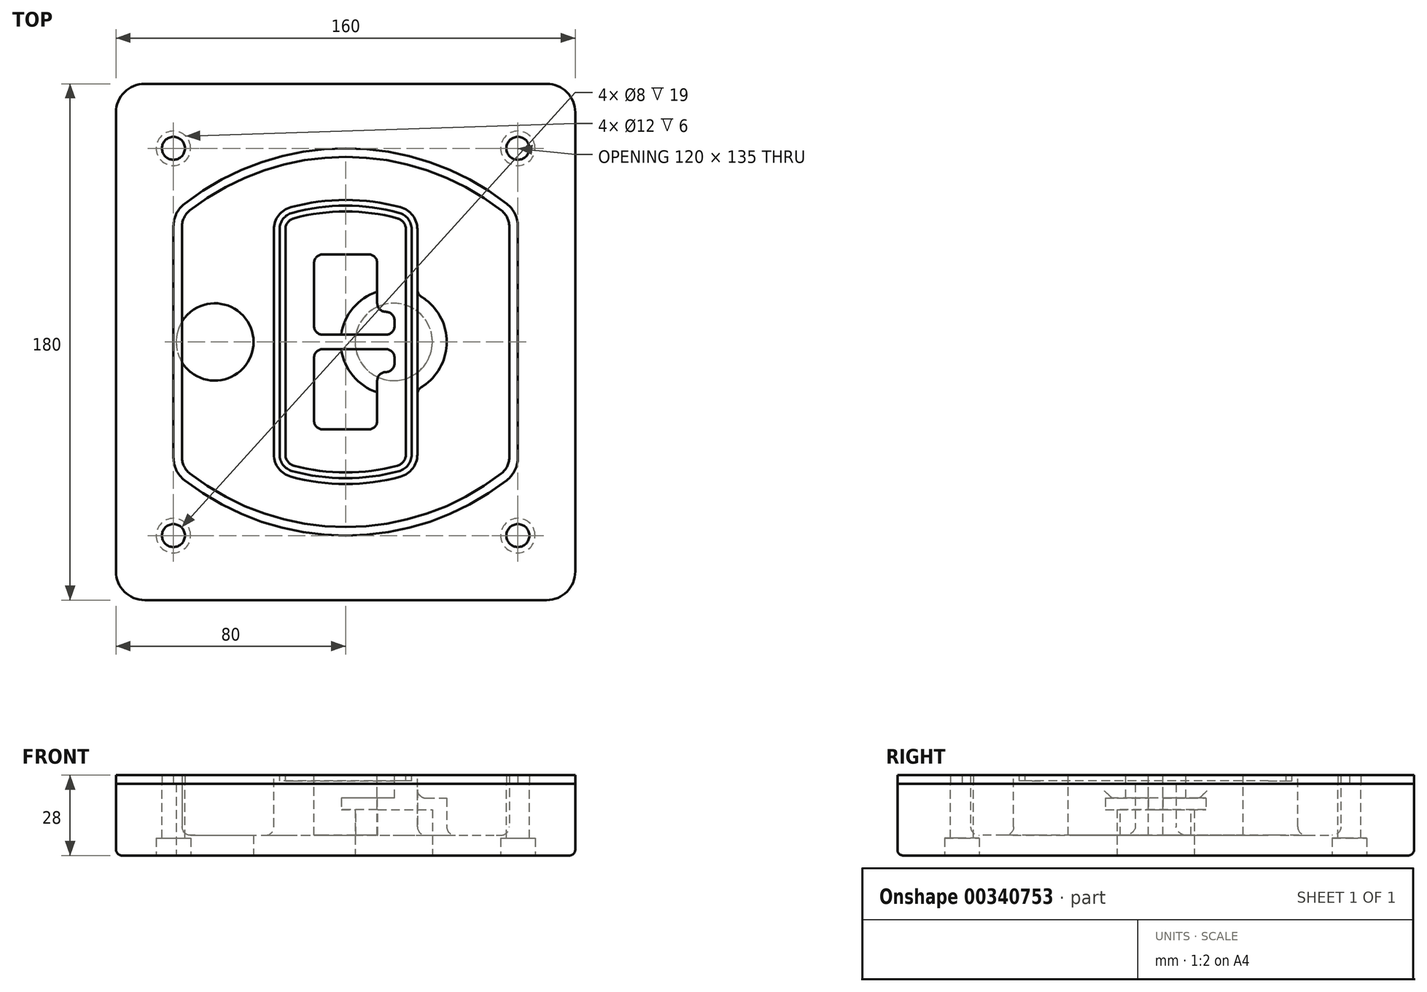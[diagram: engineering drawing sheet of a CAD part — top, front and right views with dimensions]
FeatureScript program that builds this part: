
annotation { "Feature Type Name" : "Feature", "Feature Type Description" : "" }
export const myFeature = defineFeature(function(context is Context, id is Id, definition is map)
    precondition{}
    {
        {
            var Q0;
            Q0=qCreatedBy(makeId("Top.planeOp"),FACE);
            var sketch = newSketch(context, id + "F0", { "sketchPlane" : qUnion([Q0])});
            skPoint(sketch, "E0.rect.middle", {"position": v(0, 0) * mm});
            skLineSegment(sketch, "E1.bottom", {"start": v(-70, -90) * mm, "end": v(70, -90) * mm});
            skLineSegment(sketch, "E1.top", {"start": v(-70, 90) * mm, "end": v(70, 90) * mm});
            skLineSegment(sketch, "E1.left", {"start": v(-80, -80) * mm, "end": v(-80, 80) * mm});
            skLineSegment(sketch, "E1.right", {"start": v(80, -80) * mm, "end": v(80, 80) * mm});
            skLineSegment(sketch, "E2", {"start": v(-80, 90) * mm, "end": v(80, -90) * mm, "construction": true});
            skLineSegment(sketch, "E3", {"start": v(80, 90) * mm, "end": v(-80, -90) * mm, "construction": true});
            skCircle(sketch, "E4", {"center": v(-60, 67.5) * mm, "radius": 4 * mm});
            skCircle(sketch, "E5", {"center": v(60, 67.5) * mm, "radius": 4 * mm});
            skCircle(sketch, "E6", {"center": v(60, -67.5) * mm, "radius": 4 * mm});
            skCircle(sketch, "E7", {"center": v(-60, -67.5) * mm, "radius": 4 * mm});
            skLineSegment(sketch, "E8", {"start": v(-60, 67.5) * mm, "end": v(60, 67.5) * mm, "construction": true});
            skLineSegment(sketch, "E9", {"start": v(60, 67.5) * mm, "end": v(60, -67.5) * mm, "construction": true});
            skLineSegment(sketch, "E10", {"start": v(60, -67.5) * mm, "end": v(-60, -67.5) * mm, "construction": true});
            skLineSegment(sketch, "E11", {"start": v(-60, -67.5) * mm, "end": v(-60, 67.5) * mm, "construction": true});
            skLineSegment(sketch, "E12", {"start": v(-60, 40.3) * mm, "end": v(-60, -40.3) * mm});
            skLineSegment(sketch, "E13", {"start": v(60, 40.3) * mm, "end": v(60, -40.3) * mm});
            skArc(sketch, "E14", {"start": v(56.15, 48.18) * mm, "mid": v(0, 67.5) * mm, "end": v(-56.15, 48.18) * mm});
            skArc(sketch, "E15", {"start": v(-56.15, -48.18) * mm, "mid": v(0, -67.5) * mm, "end": v(56.15, -48.18) * mm});
            skLineSegment(sketch, "E16", {"start": v(-60, 0) * mm, "end": v(60, 0) * mm, "construction": true});
            skPoint(sketch, "E17.visualSharp", {"position": v(-60, -45) * mm});
            skArc(sketch, "E17.filletArc", {"start": v(-60, -40.3) * mm, "mid": v(-58.99, -44.68) * mm, "end": v(-56.15, -48.18) * mm});
            skPoint(sketch, "E18.visualSharp", {"position": v(-60, 45) * mm});
            skArc(sketch, "E18.filletArc", {"start": v(-56.15, 48.18) * mm, "mid": v(-58.99, 44.68) * mm, "end": v(-60, 40.3) * mm});
            skPoint(sketch, "E19.visualSharp", {"position": v(60, 45) * mm});
            skArc(sketch, "E19.filletArc", {"start": v(60, 40.3) * mm, "mid": v(58.99, 44.68) * mm, "end": v(56.15, 48.18) * mm});
            skPoint(sketch, "E20.visualSharp", {"position": v(60, -45) * mm});
            skArc(sketch, "E20.filletArc", {"start": v(56.15, -48.18) * mm, "mid": v(58.99, -44.68) * mm, "end": v(60, -40.3) * mm});
            skPoint(sketch, "E21.visualSharp", {"position": v(-80, 90) * mm});
            skArc(sketch, "E21.filletArc", {"start": v(-70, 90) * mm, "mid": v(-77.07, 87.07) * mm, "end": v(-80, 80) * mm});
            skPoint(sketch, "E22.visualSharp", {"position": v(80, 90) * mm});
            skArc(sketch, "E22.filletArc", {"start": v(80, 80) * mm, "mid": v(77.07, 87.07) * mm, "end": v(70, 90) * mm});
            skPoint(sketch, "E23.visualSharp", {"position": v(80, -90) * mm});
            skArc(sketch, "E23.filletArc", {"start": v(70, -90) * mm, "mid": v(77.07, -87.07) * mm, "end": v(80, -80) * mm});
            skPoint(sketch, "E24.visualSharp", {"position": v(-80, -90) * mm});
            skArc(sketch, "E24.filletArc", {"start": v(-80, -80) * mm, "mid": v(-77.07, -87.07) * mm, "end": v(-70, -90) * mm});
            skArc(sketch, "E25.0", {"start": v(57, 40.3) * mm, "mid": v(56.3, 43.36) * mm, "end": v(54.3, 45.81) * mm});
            skLineSegment(sketch, "E25.1", {"start": v(57, 40.3) * mm, "end": v(57, -40.3) * mm});
            skArc(sketch, "E25.2", {"start": v(54.3, -45.81) * mm, "mid": v(56.3, -43.36) * mm, "end": v(57, -40.3) * mm});
            skArc(sketch, "E25.3", {"start": v(-54.3, -45.81) * mm, "mid": v(0, -64.5) * mm, "end": v(54.3, -45.81) * mm});
            skArc(sketch, "E25.4", {"start": v(-57, -40.3) * mm, "mid": v(-56.3, -43.36) * mm, "end": v(-54.3, -45.81) * mm});
            skArc(sketch, "E25.5", {"start": v(54.3, 45.81) * mm, "mid": v(0, 64.5) * mm, "end": v(-54.3, 45.81) * mm});
            skLineSegment(sketch, "E25.6", {"start": v(-57, 40.3) * mm, "end": v(-57, -40.3) * mm});
            skArc(sketch, "E25.7", {"start": v(-54.3, 45.81) * mm, "mid": v(-56.3, 43.36) * mm, "end": v(-57, 40.3) * mm});
            skArc(sketch, "E26.0", {"start": v(-58.62, 51.33) * mm, "mid": v(-62.58, 46.43) * mm, "end": v(-64, 40.3) * mm});
            skArc(sketch, "E26.1", {"start": v(58.62, 51.33) * mm, "mid": v(0, 71.5) * mm, "end": v(-58.62, 51.33) * mm});
            skArc(sketch, "E26.2", {"start": v(64, 40.3) * mm, "mid": v(62.58, 46.43) * mm, "end": v(58.62, 51.33) * mm});
            skLineSegment(sketch, "E26.3", {"start": v(64, 40.3) * mm, "end": v(64, -40.3) * mm});
            skArc(sketch, "E26.4", {"start": v(58.62, -51.33) * mm, "mid": v(62.58, -46.43) * mm, "end": v(64, -40.3) * mm});
            skLineSegment(sketch, "E26.5", {"start": v(-64, 40.3) * mm, "end": v(-64, -40.3) * mm});
            skArc(sketch, "E26.6", {"start": v(-58.62, -51.33) * mm, "mid": v(0, -71.5) * mm, "end": v(58.62, -51.33) * mm});
            skArc(sketch, "E26.7", {"start": v(-64, -40.3) * mm, "mid": v(-62.58, -46.43) * mm, "end": v(-58.62, -51.33) * mm});
            skSolve(sketch);
        }
        {
            var Q0;
            Q0=makeQuery(id+"F0.imprint","IMPRINT",FACE,{"disambiguationData":[TD([[makeQuery(id+"F0.imprint","IMPRINT",EDGE,{"derivedFrom":sQuery(id+"F0.wireOp",EDGE,"E1.bottom")}),1.0]])]});
            var Q1;
            Q1=makeQuery(id+"F0.imprint","IMPRINT",FACE,{"disambiguationData":[TD([[makeQuery(id+"F0.imprint","IMPRINT",EDGE,{"derivedFrom":sQuery(id+"F0.wireOp",EDGE,"E12")}),1.0]])]});
            var Q2;
            Q2=makeQuery(id+"F0.imprint","IMPRINT",FACE,{"disambiguationData":[TD([[makeQuery(id+"F0.imprint","IMPRINT",EDGE,{"derivedFrom":sQuery(id+"F0.wireOp",EDGE,"E25.0")}),1.0]])]});
            var Q3;
            Q3=makeQuery(id+"F0.imprint","IMPRINT",FACE,{"disambiguationData":[TD([[makeQuery(id+"F0.imprint","IMPRINT",EDGE,{"derivedFrom":sQuery(id+"F0.wireOp",EDGE,"E12")}),-1.0]])]});
            extrude(context, id + "F1", {"entities" : qUnion([Q0, Q1, Q2, Q3]), "oppositeDirection" : true, "depth" : 25 * mm});
        }
        {
            var Q0;
            Q0=makeQuery(id+"F0.imprint","IMPRINT",FACE,{"disambiguationData":[TD([[makeQuery(id+"F0.imprint","IMPRINT",EDGE,{"derivedFrom":sQuery(id+"F0.wireOp",EDGE,"E12")}),1.0]])]});
            extrude(context, id + "F2", {"entities" : qUnion([Q0]), "operationType" : NewBodyOperationType.ADD, "depth" : 3 * mm});
        }
        {
            var Q0;
            Q0=makeQuery(id+"F0.imprint","IMPRINT",FACE,{"disambiguationData":[TD([[makeQuery(id+"F0.imprint","IMPRINT",EDGE,{"derivedFrom":sQuery(id+"F0.wireOp",EDGE,"E25.0")}),1.0]])]});
            extrude(context, id + "F3", {"entities" : qUnion([Q0]), "operationType" : NewBodyOperationType.REMOVE, "oppositeDirection" : true, "depth" : 18 * mm});
        }
        {
            var Q0;
            Q0=makeQuery(id+"F2.opExtrude","CAP_FACE",FACE,{"disambiguationData":[OSD([sQuery(id+"F0.wireOp",EDGE,"E12"),sQuery(id+"F0.wireOp",EDGE,"E13"),sQuery(id+"F0.wireOp",EDGE,"E14"),sQuery(id+"F0.wireOp",EDGE,"E15"),sQuery(id+"F0.wireOp",EDGE,"E17.filletArc"),sQuery(id+"F0.wireOp",EDGE,"E18.filletArc"),sQuery(id+"F0.wireOp",EDGE,"E19.filletArc"),sQuery(id+"F0.wireOp",EDGE,"E20.filletArc"),sQuery(id+"F0.wireOp",EDGE,"E25.0"),sQuery(id+"F0.wireOp",EDGE,"E25.1"),sQuery(id+"F0.wireOp",EDGE,"E25.2"),sQuery(id+"F0.wireOp",EDGE,"E25.3"),sQuery(id+"F0.wireOp",EDGE,"E25.4"),sQuery(id+"F0.wireOp",EDGE,"E25.5"),sQuery(id+"F0.wireOp",EDGE,"E25.6"),sQuery(id+"F0.wireOp",EDGE,"E25.7")])],"isStart":false});
            var sketch = newSketch(context, id + "F4", { "sketchPlane" : qUnion([Q0])});
            skArc(sketch, "E27.0", {"start": v(-19.08, -46.97) * mm, "mid": v(0, -49.5) * mm, "end": v(19.08, -46.97) * mm});
            skArc(sketch, "E28.0", {"start": v(19.08, 46.97) * mm, "mid": v(0, 49.5) * mm, "end": v(-19.08, 46.97) * mm});
            skLineSegment(sketch, "E29", {"start": v(-25, 39.25) * mm, "end": v(-25, -39.25) * mm});
            skLineSegment(sketch, "E30", {"start": v(25, 39.25) * mm, "end": v(25, -39.25) * mm});
            skLineSegment(sketch, "E31", {"start": v(-25, 45.1) * mm, "end": v(25, 45.1) * mm, "construction": true});
            skLineSegment(sketch, "E32", {"start": v(-25, -45.1) * mm, "end": v(25, -45.1) * mm, "construction": true});
            skPoint(sketch, "E33.visualSharp", {"position": v(-25, 45.1) * mm});
            skArc(sketch, "E33.filletArc", {"start": v(-19.08, 46.97) * mm, "mid": v(-23.35, 44.11) * mm, "end": v(-25, 39.25) * mm});
            skPoint(sketch, "E34.visualSharp", {"position": v(25, 45.1) * mm});
            skArc(sketch, "E34.filletArc", {"start": v(25, 39.25) * mm, "mid": v(23.35, 44.11) * mm, "end": v(19.08, 46.97) * mm});
            skPoint(sketch, "E35.visualSharp", {"position": v(25, -45.1) * mm});
            skArc(sketch, "E35.filletArc", {"start": v(19.08, -46.97) * mm, "mid": v(23.35, -44.11) * mm, "end": v(25, -39.25) * mm});
            skPoint(sketch, "E36.visualSharp", {"position": v(-25, -45.1) * mm});
            skArc(sketch, "E36.filletArc", {"start": v(-25, -39.25) * mm, "mid": v(-23.35, -44.11) * mm, "end": v(-19.08, -46.97) * mm});
            skArc(sketch, "E37.0", {"start": v(54.3, 45.81) * mm, "mid": v(0, 64.5) * mm, "end": v(-54.3, 45.81) * mm});
            skArc(sketch, "E37.1", {"start": v(-54.3, 45.81) * mm, "mid": v(-56.3, 43.36) * mm, "end": v(-57, 40.3) * mm});
            skLineSegment(sketch, "E37.2", {"start": v(-57, 40.3) * mm, "end": v(-57, -40.3) * mm});
            skArc(sketch, "E37.3", {"start": v(-57, -40.3) * mm, "mid": v(-56.3, -43.36) * mm, "end": v(-54.3, -45.81) * mm});
            skArc(sketch, "E37.4", {"start": v(-54.3, -45.81) * mm, "mid": v(0, -64.5) * mm, "end": v(54.3, -45.81) * mm});
            skArc(sketch, "E37.5", {"start": v(54.3, -45.81) * mm, "mid": v(56.3, -43.36) * mm, "end": v(57, -40.3) * mm});
            skLineSegment(sketch, "E37.6", {"start": v(57, 40.3) * mm, "end": v(57, -40.3) * mm});
            skArc(sketch, "E37.7", {"start": v(57, 40.3) * mm, "mid": v(56.3, 43.36) * mm, "end": v(54.3, 45.81) * mm});
            skLineSegment(sketch, "E38.0", {"start": v(23, 39.25) * mm, "end": v(23, -39.25) * mm});
            skArc(sketch, "E38.1", {"start": v(18.56, -45.04) * mm, "mid": v(21.76, -42.9) * mm, "end": v(23, -39.25) * mm});
            skArc(sketch, "E38.2", {"start": v(-18.56, -45.04) * mm, "mid": v(0, -47.5) * mm, "end": v(18.56, -45.04) * mm});
            skArc(sketch, "E38.3", {"start": v(-23, -39.25) * mm, "mid": v(-21.76, -42.9) * mm, "end": v(-18.56, -45.04) * mm});
            skLineSegment(sketch, "E38.4", {"start": v(-23, 39.25) * mm, "end": v(-23, -39.25) * mm});
            skArc(sketch, "E38.5", {"start": v(23, 39.25) * mm, "mid": v(21.76, 42.9) * mm, "end": v(18.56, 45.04) * mm});
            skArc(sketch, "E38.6", {"start": v(-18.56, 45.04) * mm, "mid": v(-21.76, 42.9) * mm, "end": v(-23, 39.25) * mm});
            skArc(sketch, "E38.7", {"start": v(18.56, 45.04) * mm, "mid": v(0, 47.5) * mm, "end": v(-18.56, 45.04) * mm});
            skArc(sketch, "E39.0", {"start": v(21, 39.25) * mm, "mid": v(20.18, 41.68) * mm, "end": v(18.04, 43.1) * mm});
            skLineSegment(sketch, "E39.1", {"start": v(21, 39.25) * mm, "end": v(21, -39.25) * mm});
            skArc(sketch, "E39.2", {"start": v(18.04, -43.1) * mm, "mid": v(20.18, -41.68) * mm, "end": v(21, -39.25) * mm});
            skArc(sketch, "E39.3", {"start": v(-18.04, -43.1) * mm, "mid": v(0, -45.5) * mm, "end": v(18.04, -43.1) * mm});
            skArc(sketch, "E39.4", {"start": v(-21, -39.25) * mm, "mid": v(-20.18, -41.68) * mm, "end": v(-18.04, -43.1) * mm});
            skArc(sketch, "E39.5", {"start": v(18.04, 43.1) * mm, "mid": v(0, 45.5) * mm, "end": v(-18.04, 43.1) * mm});
            skLineSegment(sketch, "E39.6", {"start": v(-21, 39.25) * mm, "end": v(-21, -39.25) * mm});
            skArc(sketch, "E39.7", {"start": v(-18.04, 43.1) * mm, "mid": v(-20.18, 41.68) * mm, "end": v(-21, 39.25) * mm});
            skLineSegment(sketch, "E40", {"start": v(-25, 0) * mm, "end": v(25, 0) * mm, "construction": true});
            skLineSegment(sketch, "E41", {"start": v(-11, 5.5) * mm, "end": v(-11, 27.5) * mm});
            skLineSegment(sketch, "E42", {"start": v(-8, 30.5) * mm, "end": v(8, 30.5) * mm});
            skLineSegment(sketch, "E43", {"start": v(11, 27.5) * mm, "end": v(11, 13.5) * mm});
            skLineSegment(sketch, "E44", {"start": v(14, 10.5) * mm, "end": v(14, 10.5) * mm});
            skLineSegment(sketch, "E45", {"start": v(17, 7.5) * mm, "end": v(17, 5.5) * mm});
            skLineSegment(sketch, "E46", {"start": v(14, 2.5) * mm, "end": v(-8, 2.5) * mm});
            skPoint(sketch, "E47.visualSharp", {"position": v(-11, 30.5) * mm});
            skArc(sketch, "E47.filletArc", {"start": v(-8, 30.5) * mm, "mid": v(-10.12, 29.62) * mm, "end": v(-11, 27.5) * mm});
            skPoint(sketch, "E48.visualSharp", {"position": v(11, 30.5) * mm});
            skArc(sketch, "E48.filletArc", {"start": v(11, 27.5) * mm, "mid": v(10.12, 29.62) * mm, "end": v(8, 30.5) * mm});
            skPoint(sketch, "E49.visualSharp", {"position": v(11, 10.5) * mm});
            skArc(sketch, "E49.filletArc", {"start": v(11, 13.5) * mm, "mid": v(11.88, 11.38) * mm, "end": v(14, 10.5) * mm});
            skPoint(sketch, "E50.visualSharp", {"position": v(17, 10.5) * mm});
            skArc(sketch, "E50.filletArc", {"start": v(17, 7.5) * mm, "mid": v(16.12, 9.62) * mm, "end": v(14, 10.5) * mm});
            skPoint(sketch, "E51.visualSharp", {"position": v(17, 2.5) * mm});
            skArc(sketch, "E51.filletArc", {"start": v(14, 2.5) * mm, "mid": v(16.12, 3.38) * mm, "end": v(17, 5.5) * mm});
            skPoint(sketch, "E52.visualSharp", {"position": v(-11, 2.5) * mm});
            skArc(sketch, "E52.filletArc", {"start": v(-11, 5.5) * mm, "mid": v(-10.12, 3.38) * mm, "end": v(-8, 2.5) * mm});
            skLineSegment(sketch, "E53.0.MirrorCS", {"start": v(14, -2.5) * mm, "end": v(-8, -2.5) * mm});
            skArc(sketch, "E54.0.MirrorCS", {"start": v(-11, -5.5) * mm, "mid": v(-10.12, -3.38) * mm, "end": v(-8, -2.5) * mm});
            skLineSegment(sketch, "E55.0.MirrorCS", {"start": v(-11, -5.5) * mm, "end": v(-11, -27.5) * mm});
            skArc(sketch, "E56.0.MirrorCS", {"start": v(-8, -30.5) * mm, "mid": v(-10.12, -29.62) * mm, "end": v(-11, -27.5) * mm});
            skLineSegment(sketch, "E57.0.MirrorCS", {"start": v(-8, -30.5) * mm, "end": v(8, -30.5) * mm});
            skArc(sketch, "E58.0.MirrorCS", {"start": v(11, -27.5) * mm, "mid": v(10.12, -29.62) * mm, "end": v(8, -30.5) * mm});
            skLineSegment(sketch, "E59.0.MirrorCS", {"start": v(11, -27.5) * mm, "end": v(11, -13.5) * mm});
            skArc(sketch, "E60.0.MirrorCS", {"start": v(11, -13.5) * mm, "mid": v(11.88, -11.38) * mm, "end": v(14, -10.5) * mm});
            skArc(sketch, "E61.0.MirrorCS", {"start": v(17, -7.5) * mm, "mid": v(16.12, -9.62) * mm, "end": v(14, -10.5) * mm});
            skLineSegment(sketch, "E62.0.MirrorCS", {"start": v(17, -7.5) * mm, "end": v(17, -5.5) * mm});
            skArc(sketch, "E63.0.MirrorCS", {"start": v(14, -2.5) * mm, "mid": v(16.12, -3.38) * mm, "end": v(17, -5.5) * mm});
            skSolve(sketch);
        }
        {
            var Q0;
            Q0=makeQuery(id+"F4.imprint","IMPRINT",FACE,{"disambiguationData":[TD([[makeQuery(id+"F4.imprint","IMPRINT",EDGE,{"derivedFrom":sQuery(id+"F4.wireOp",EDGE,"E27.0")}),1.0]])]});
            var Q1;
            Q1=makeQuery(id+"F4.imprint","IMPRINT",FACE,{"disambiguationData":[TD([[makeQuery(id+"F4.imprint","IMPRINT",EDGE,{"derivedFrom":sQuery(id+"F4.wireOp",EDGE,"E38.0")}),-1.0]])]});
            var Q2;
            Q2=makeQuery(id+"F4.imprint","IMPRINT",FACE,{"disambiguationData":[TD([[makeQuery(id+"F4.imprint","IMPRINT",EDGE,{"derivedFrom":sQuery(id+"F4.wireOp",EDGE,"E39.0")}),1.0]])]});
            extrude(context, id + "F5", {"entities" : qUnion([Q0, Q1, Q2]), "operationType" : NewBodyOperationType.ADD, "endBound" : BoundingType.UP_TO_NEXT, "oppositeDirection" : true, "depth" : 25 * mm});
        }
        {
            var Q0;
            Q0=makeQuery(id+"F4.imprint","IMPRINT",FACE,{"disambiguationData":[TD([[makeQuery(id+"F4.imprint","IMPRINT",EDGE,{"derivedFrom":sQuery(id+"F4.wireOp",EDGE,"E38.0")}),-1.0]])]});
            extrude(context, id + "F6", {"entities" : qUnion([Q0]), "operationType" : NewBodyOperationType.REMOVE, "oppositeDirection" : true, "depth" : 2 * mm});
        }
        {
            var Q0;
            Q0=makeQuery(id+"F1.opExtrude","CAP_FACE",FACE,{"disambiguationData":[OSD([sQuery(id+"F0.wireOp",EDGE,"E1.bottom"),sQuery(id+"F0.wireOp",EDGE,"E1.top"),sQuery(id+"F0.wireOp",EDGE,"E1.left"),sQuery(id+"F0.wireOp",EDGE,"E1.right"),sQuery(id+"F0.wireOp",EDGE,"E4"),sQuery(id+"F0.wireOp",EDGE,"E5"),sQuery(id+"F0.wireOp",EDGE,"E6"),sQuery(id+"F0.wireOp",EDGE,"E7"),sQuery(id+"F0.wireOp",EDGE,"E21.filletArc"),sQuery(id+"F0.wireOp",EDGE,"E22.filletArc"),sQuery(id+"F0.wireOp",EDGE,"E23.filletArc"),sQuery(id+"F0.wireOp",EDGE,"E24.filletArc")])],"isStart":false});
            var sketch = newSketch(context, id + "F7", { "sketchPlane" : qUnion([Q0])});
            skCircle(sketch, "E64", {"center": v(16.76, 0) * mm, "radius": 13.47 * mm});
            skCircle(sketch, "E65", {"center": v(-45.56, 0) * mm, "radius": 13.47 * mm});
            skLineSegment(sketch, "E66", {"start": v(80, 0) * mm, "end": v(-80, 0) * mm});
            skCircle(sketch, "E67", {"center": v(16.76, 0) * mm, "radius": 18.47 * mm});
            skCircle(sketch, "E68", {"center": v(60, -67.5) * mm, "radius": 6 * mm});
            skCircle(sketch, "E69", {"center": v(-60, -67.5) * mm, "radius": 6 * mm});
            skCircle(sketch, "E70", {"center": v(-60, 67.5) * mm, "radius": 6 * mm});
            skCircle(sketch, "E71", {"center": v(60, 67.5) * mm, "radius": 6 * mm});
            skSolve(sketch);
        }
        {
            var Q0;
            {var subQ1=sQuery(id+"F7.wireOp",EDGE,"E66");var subQ4=sQuery(id+"F7.wireOp",EDGE,"E64");var subQ6=makeQuery(id+"F7.imprint","INTERSECT",VERTEX,{"disambiguationData":[OD(0.0)],"derivedFrom":[subQ4,subQ1]});Q0=makeQuery(id+"F7.imprint","IMPRINT",FACE,{"disambiguationData":[TD([[makeQuery(id+"F7.imprint","IMPRINT",EDGE,{"disambiguationData":[TD([[subQ6,-1.0]])],"derivedFrom":subQ4}),-1.0]])]});}
            var Q1;
            {var subQ0=sQuery(id+"F7.wireOp",EDGE,"E66");var subQ1=sQuery(id+"F7.wireOp",EDGE,"E64");var subQ3=makeQuery(id+"F7.imprint","INTERSECT",VERTEX,{"disambiguationData":[OD(0.0)],"derivedFrom":[subQ1,subQ0]});Q1=makeQuery(id+"F7.imprint","IMPRINT",FACE,{"disambiguationData":[TD([[makeQuery(id+"F7.imprint","IMPRINT",EDGE,{"disambiguationData":[TD([[subQ3,-1.0]])],"derivedFrom":subQ1}),1.0]])]});}
            var Q2;
            {var subQ0=sQuery(id+"F7.wireOp",EDGE,"E66");var subQ1=sQuery(id+"F7.wireOp",EDGE,"E64");var subQ3=makeQuery(id+"F7.imprint","INTERSECT",VERTEX,{"disambiguationData":[OD(0.0)],"derivedFrom":[subQ1,subQ0]});Q2=makeQuery(id+"F7.imprint","IMPRINT",FACE,{"disambiguationData":[TD([[makeQuery(id+"F7.imprint","IMPRINT",EDGE,{"disambiguationData":[TD([[subQ3,1.0]])],"derivedFrom":subQ1}),1.0]])]});}
            var Q3;
            {var subQ1=sQuery(id+"F7.wireOp",EDGE,"E66");var subQ4=sQuery(id+"F7.wireOp",EDGE,"E64");var subQ6=makeQuery(id+"F7.imprint","INTERSECT",VERTEX,{"disambiguationData":[OD(0.0)],"derivedFrom":[subQ4,subQ1]});Q3=makeQuery(id+"F7.imprint","IMPRINT",FACE,{"disambiguationData":[TD([[makeQuery(id+"F7.imprint","IMPRINT",EDGE,{"disambiguationData":[TD([[subQ6,1.0]])],"derivedFrom":subQ4}),-1.0]])]});}
            extrude(context, id + "F8", {"entities" : qUnion([Q0, Q1, Q2, Q3]), "operationType" : NewBodyOperationType.ADD, "oppositeDirection" : true, "depth" : 20 * mm});
        }
        {
            var Q0;
            {var subQ0=sQuery(id+"F7.wireOp",EDGE,"E66");var subQ1=sQuery(id+"F7.wireOp",EDGE,"E64");var subQ3=makeQuery(id+"F7.imprint","INTERSECT",VERTEX,{"disambiguationData":[OD(0.0)],"derivedFrom":[subQ1,subQ0]});Q0=makeQuery(id+"F7.imprint","IMPRINT",FACE,{"disambiguationData":[TD([[makeQuery(id+"F7.imprint","IMPRINT",EDGE,{"disambiguationData":[TD([[subQ3,-1.0]])],"derivedFrom":subQ1}),1.0]])]});}
            var Q1;
            {var subQ0=sQuery(id+"F7.wireOp",EDGE,"E66");var subQ1=sQuery(id+"F7.wireOp",EDGE,"E64");var subQ3=makeQuery(id+"F7.imprint","INTERSECT",VERTEX,{"disambiguationData":[OD(0.0)],"derivedFrom":[subQ1,subQ0]});Q1=makeQuery(id+"F7.imprint","IMPRINT",FACE,{"disambiguationData":[TD([[makeQuery(id+"F7.imprint","IMPRINT",EDGE,{"disambiguationData":[TD([[subQ3,1.0]])],"derivedFrom":subQ1}),1.0]])]});}
            extrude(context, id + "F9", {"entities" : qUnion([Q0, Q1]), "operationType" : NewBodyOperationType.REMOVE, "oppositeDirection" : true, "depth" : 16 * mm});
        }
        {
            var Q0;
            {var subQ0=sQuery(id+"F7.wireOp",EDGE,"E66");var subQ1=sQuery(id+"F7.wireOp",EDGE,"E65");var subQ3=makeQuery(id+"F7.imprint","INTERSECT",VERTEX,{"disambiguationData":[OD(0.0)],"derivedFrom":[subQ1,subQ0]});Q0=makeQuery(id+"F7.imprint","IMPRINT",FACE,{"disambiguationData":[TD([[makeQuery(id+"F7.imprint","IMPRINT",EDGE,{"disambiguationData":[TD([[subQ3,-1.0]])],"derivedFrom":subQ1}),1.0]])]});}
            var Q1;
            {var subQ0=sQuery(id+"F7.wireOp",EDGE,"E66");var subQ1=sQuery(id+"F7.wireOp",EDGE,"E65");var subQ3=makeQuery(id+"F7.imprint","INTERSECT",VERTEX,{"disambiguationData":[OD(0.0)],"derivedFrom":[subQ1,subQ0]});Q1=makeQuery(id+"F7.imprint","IMPRINT",FACE,{"disambiguationData":[TD([[makeQuery(id+"F7.imprint","IMPRINT",EDGE,{"disambiguationData":[TD([[subQ3,1.0]])],"derivedFrom":subQ1}),1.0]])]});}
            extrude(context, id + "F10", {"entities" : qUnion([Q0, Q1]), "operationType" : NewBodyOperationType.REMOVE, "oppositeDirection" : true, "depth" : 25 * mm});
        }
        {
            var Q0;
            Q0=makeQuery(id+"F7.imprint","IMPRINT",FACE,{"disambiguationData":[TD([[makeQuery(id+"F7.imprint","IMPRINT",EDGE,{"derivedFrom":sQuery(id+"F7.wireOp",EDGE,"E68")}),1.0]])]});
            var Q1;
            Q1=makeQuery(id+"F7.imprint","IMPRINT",FACE,{"disambiguationData":[TD([[makeQuery(id+"F7.imprint","IMPRINT",EDGE,{"derivedFrom":makeQuery(id+"F1.opExtrude","CAP_EDGE",EDGE,{"disambiguationData":[OSD([sQuery(id+"F0.wireOp",EDGE,"E5")])],"isStart":false})}),-1.0]])]});
            var Q2;
            Q2=makeQuery(id+"F7.imprint","IMPRINT",FACE,{"disambiguationData":[TD([[makeQuery(id+"F7.imprint","IMPRINT",EDGE,{"derivedFrom":sQuery(id+"F7.wireOp",EDGE,"E69")}),1.0]])]});
            var Q3;
            Q3=makeQuery(id+"F7.imprint","IMPRINT",FACE,{"disambiguationData":[TD([[makeQuery(id+"F7.imprint","IMPRINT",EDGE,{"derivedFrom":makeQuery(id+"F1.opExtrude","CAP_EDGE",EDGE,{"disambiguationData":[OSD([sQuery(id+"F0.wireOp",EDGE,"E4")])],"isStart":false})}),-1.0]])]});
            var Q4;
            Q4=makeQuery(id+"F7.imprint","IMPRINT",FACE,{"disambiguationData":[TD([[makeQuery(id+"F7.imprint","IMPRINT",EDGE,{"derivedFrom":sQuery(id+"F7.wireOp",EDGE,"E70")}),1.0]])]});
            var Q5;
            Q5=makeQuery(id+"F7.imprint","IMPRINT",FACE,{"disambiguationData":[TD([[makeQuery(id+"F7.imprint","IMPRINT",EDGE,{"derivedFrom":makeQuery(id+"F1.opExtrude","CAP_EDGE",EDGE,{"disambiguationData":[OSD([sQuery(id+"F0.wireOp",EDGE,"E7")])],"isStart":false})}),-1.0]])]});
            var Q6;
            Q6=makeQuery(id+"F7.imprint","IMPRINT",FACE,{"disambiguationData":[TD([[makeQuery(id+"F7.imprint","IMPRINT",EDGE,{"derivedFrom":sQuery(id+"F7.wireOp",EDGE,"E71")}),1.0]])]});
            var Q7;
            Q7=makeQuery(id+"F7.imprint","IMPRINT",FACE,{"disambiguationData":[TD([[makeQuery(id+"F7.imprint","IMPRINT",EDGE,{"derivedFrom":makeQuery(id+"F1.opExtrude","CAP_EDGE",EDGE,{"disambiguationData":[OSD([sQuery(id+"F0.wireOp",EDGE,"E6")])],"isStart":false})}),-1.0]])]});
            extrude(context, id + "F11", {"entities" : qUnion([Q0, Q1, Q2, Q3, Q4, Q5, Q6, Q7]), "operationType" : NewBodyOperationType.REMOVE, "oppositeDirection" : true, "depth" : 6 * mm});
        }
        {
            var Q0;
            Q0=makeQuery(id+"F9.boolean.opBoolean","COPY",FACE,{"derivedFrom":makeQuery(id+"F9.opExtrude","CAP_FACE",FACE,{"disambiguationData":[OSD([sQuery(id+"F7.wireOp",EDGE,"E64")])],"isStart":false})});
            var sketch = newSketch(context, id + "F12", { "sketchPlane" : qUnion([Q0])});
            skArc(sketch, "E72.0", {"start": v(11, 17.55) * mm, "mid": v(2.57, 11.82) * mm, "end": v(-1.54, 2.5) * mm});
            skArc(sketch, "E72.1", {"start": v(-1.54, -2.5) * mm, "mid": v(2.57, -11.82) * mm, "end": v(11, -17.55) * mm});
            skLineSegment(sketch, "E73", {"start": v(-1.54, -2.5) * mm, "end": v(14, -2.5) * mm});
            skLineSegment(sketch, "E74.0", {"start": v(14, 2.5) * mm, "end": v(-1.54, 2.5) * mm});
            skArc(sketch, "E74.1", {"start": v(14, 2.5) * mm, "mid": v(16.12, 3.38) * mm, "end": v(17, 5.5) * mm});
            skLineSegment(sketch, "E74.2", {"start": v(17, 7.5) * mm, "end": v(17, 5.5) * mm});
            skArc(sketch, "E74.3", {"start": v(17, 7.5) * mm, "mid": v(16.12, 9.62) * mm, "end": v(14, 10.5) * mm});
            skArc(sketch, "E74.4", {"start": v(11, 13.5) * mm, "mid": v(11.88, 11.38) * mm, "end": v(14, 10.5) * mm});
            skLineSegment(sketch, "E74.5", {"start": v(11, 17.55) * mm, "end": v(11, 13.5) * mm});
            skLineSegment(sketch, "E74.7", {"start": v(14, -2.5) * mm, "end": v(-1.54, -2.5) * mm});
            skArc(sketch, "E74.8", {"start": v(14, -2.5) * mm, "mid": v(16.12, -3.38) * mm, "end": v(17, -5.5) * mm});
            skLineSegment(sketch, "E74.9", {"start": v(17, -7.5) * mm, "end": v(17, -5.5) * mm});
            skArc(sketch, "E74.10", {"start": v(17, -7.5) * mm, "mid": v(16.12, -9.62) * mm, "end": v(14, -10.5) * mm});
            skArc(sketch, "E74.11", {"start": v(11, -13.5) * mm, "mid": v(11.88, -11.38) * mm, "end": v(14, -10.5) * mm});
            skLineSegment(sketch, "E74.12", {"start": v(11, -17.55) * mm, "end": v(11, -13.5) * mm});
            skPoint(sketch, "E75.orphan", {"position": v(11, -27.5) * mm});
            skPoint(sketch, "E76.orphan", {"position": v(-8, -2.5) * mm});
            skPoint(sketch, "E77.orphan", {"position": v(-8, 2.5) * mm});
            skPoint(sketch, "E78.orphan", {"position": v(11, 27.5) * mm});
            skSolve(sketch);
        }
        {
            var Q0;
            {var subQ7=sQuery(id+"F12.wireOp",EDGE,"E72.0");var subQ14=sQuery(id+"F12.wireOp",EDGE,"E72.1");var subQ16=sQuery(id+"F12.wireOp",EDGE,"E74.1");var subQ18=sQuery(id+"F12.wireOp",EDGE,"E74.8");Q0=qUnion([makeQuery(id+"F12.imprint","IMPRINT",FACE,{"disambiguationData":[TD([[makeQuery(id+"F12.imprint","IMPRINT",EDGE,{"derivedFrom":subQ7}),1.0]])]}),makeQuery(id+"F12.imprint","IMPRINT",FACE,{"disambiguationData":[TD([[makeQuery(id+"F12.imprint","IMPRINT",EDGE,{"derivedFrom":subQ14}),1.0]])]}),makeQuery(id+"F12.imprint","IMPRINT",FACE,{"disambiguationData":[TD([[makeQuery(id+"F12.imprint","IMPRINT",EDGE,{"derivedFrom":subQ16}),1.0]])]}),makeQuery(id+"F12.imprint","IMPRINT",FACE,{"disambiguationData":[TD([[makeQuery(id+"F12.imprint","IMPRINT",EDGE,{"derivedFrom":subQ18}),-1.0]])]})]);}
            var Q1;
            Q1=makeQuery(id+"F5.boolean.opBoolean","SPLIT",FACE,{"disambiguationData":[TD([makeQuery(id+"F5.opExtrude","SWEPT_FACE",FACE,{"disambiguationData":[OSD([sQuery(id+"F4.wireOp",EDGE,"E41")])]})])],"derivedFrom":makeQuery(id+"F3.boolean.opBoolean","COPY",FACE,{"derivedFrom":makeQuery(id+"F3.opExtrude","CAP_FACE",FACE,{"disambiguationData":[OSD([sQuery(id+"F0.wireOp",EDGE,"E25.0"),sQuery(id+"F0.wireOp",EDGE,"E25.1"),sQuery(id+"F0.wireOp",EDGE,"E25.2"),sQuery(id+"F0.wireOp",EDGE,"E25.3"),sQuery(id+"F0.wireOp",EDGE,"E25.4"),sQuery(id+"F0.wireOp",EDGE,"E25.5"),sQuery(id+"F0.wireOp",EDGE,"E25.6"),sQuery(id+"F0.wireOp",EDGE,"E25.7")])],"isStart":false})})});
            extrude(context, id + "F13", {"entities" : qUnion([Q0]), "operationType" : NewBodyOperationType.REMOVE, "endBound" : BoundingType.UP_TO_SURFACE, "endBoundEntityFace" : qUnion([Q1]), "depth" : 25 * mm});
        }
        {
            var Q0;
            Q0=makeQuery(id+"F3.boolean.opBoolean","COPY",EDGE,{"derivedFrom":makeQuery(id+"F3.opExtrude","CAP_EDGE",EDGE,{"disambiguationData":[OSD([sQuery(id+"F0.wireOp",EDGE,"E25.6")])],"isStart":false})});
            var Q1;
            Q1=makeQuery(id+"F8.boolean.opBoolean","INTERSECT",EDGE,{"derivedFrom":[makeQuery(id+"F5.opExtrude","SWEPT_FACE",FACE,{"disambiguationData":[OSD([sQuery(id+"F4.wireOp",EDGE,"E30")])]}),makeQuery(id+"F8.opExtrude","CAP_FACE",FACE,{"disambiguationData":[OSD([sQuery(id+"F7.wireOp",EDGE,"E67")])],"isStart":false})]});
            var Q2;
            Q2=makeQuery(id+"F8.boolean.opBoolean","INTERSECT",EDGE,{"disambiguationData":[OD(1.0)],"derivedFrom":[makeQuery(id+"F5.opExtrude","SWEPT_FACE",FACE,{"disambiguationData":[OSD([sQuery(id+"F4.wireOp",EDGE,"E30")])]}),makeQuery(id+"F8.opExtrude","SWEPT_FACE",FACE,{"disambiguationData":[OSD([sQuery(id+"F7.wireOp",EDGE,"E67")])]})]});
            var Q3;
            {var subQ0=sQuery(id+"F4.wireOp",EDGE,"E30");Q3=makeQuery(id+"F8.boolean.opBoolean","SPLIT",EDGE,{"disambiguationData":[TD([makeQuery(id+"F5.opExtrude","SWEPT_FACE",FACE,{"disambiguationData":[OSD([sQuery(id+"F4.wireOp",EDGE,"E35.filletArc")])]})])],"derivedFrom":makeQuery(id+"F5.opExtrude","CAP_EDGE",EDGE,{"disambiguationData":[OSD([subQ0])],"isStart":false})});}
            var Q4;
            {var subQ0=sQuery(id+"F0.wireOp",EDGE,"E25.7");var subQ1=sQuery(id+"F0.wireOp",EDGE,"E25.1");var subQ2=sQuery(id+"F0.wireOp",EDGE,"E25.6");var subQ3=sQuery(id+"F0.wireOp",EDGE,"E25.5");var subQ4=sQuery(id+"F0.wireOp",EDGE,"E25.4");var subQ5=sQuery(id+"F0.wireOp",EDGE,"E25.0");var subQ6=sQuery(id+"F0.wireOp",EDGE,"E25.2");var subQ7=sQuery(id+"F0.wireOp",EDGE,"E25.3");Q4=makeQuery(id+"F8.boolean.opBoolean","INTERSECT",EDGE,{"derivedFrom":[makeQuery(id+"F5.boolean.opBoolean","SPLIT",FACE,{"disambiguationData":[TD([makeQuery(id+"F2.opExtrude","SWEPT_FACE",FACE,{"disambiguationData":[OSD([subQ5])]})])],"derivedFrom":makeQuery(id+"F3.boolean.opBoolean","COPY",FACE,{"derivedFrom":makeQuery(id+"F3.opExtrude","CAP_FACE",FACE,{"disambiguationData":[OSD([subQ5,subQ1,subQ6,subQ7,subQ4,subQ3,subQ2,subQ0])],"isStart":false})})}),makeQuery(id+"F8.opExtrude","SWEPT_FACE",FACE,{"disambiguationData":[OSD([sQuery(id+"F7.wireOp",EDGE,"E67")])]})]});}
            var Q5;
            Q5=makeQuery(id+"F8.boolean.opBoolean","INTERSECT",EDGE,{"disambiguationData":[OD(0.0)],"derivedFrom":[makeQuery(id+"F5.opExtrude","SWEPT_FACE",FACE,{"disambiguationData":[OSD([sQuery(id+"F4.wireOp",EDGE,"E30")])]}),makeQuery(id+"F8.opExtrude","SWEPT_FACE",FACE,{"disambiguationData":[OSD([sQuery(id+"F7.wireOp",EDGE,"E67")])]})]});
            fillet(context, id + "F14", {"entities" : qUnion([Q0, Q1, Q2, Q3, Q4, Q5]), "radius" : 3 * mm, "tangentPropagation" : true, "allowEdgeOverflow" : false});
        }
        {
            var Q0;
            Q0=makeQuery(id+"F1.opExtrude","CAP_EDGE",EDGE,{"disambiguationData":[OSD([sQuery(id+"F0.wireOp",EDGE,"E1.bottom")])],"isStart":false});
            fillet(context, id + "F15", {"entities" : qUnion([Q0]), "radius" : 2 * mm, "tangentPropagation" : true, "allowEdgeOverflow" : false});
        }
        {
            var Q0;
            {var subQ0=sQuery(id+"F0.wireOp",EDGE,"E21.filletArc");var subQ1=sQuery(id+"F0.wireOp",EDGE,"E7");var subQ2=sQuery(id+"F0.wireOp",EDGE,"E6");var subQ3=sQuery(id+"F0.wireOp",EDGE,"E5");var subQ4=sQuery(id+"F0.wireOp",EDGE,"E4");var subQ5=sQuery(id+"F0.wireOp",EDGE,"E22.filletArc");var subQ6=sQuery(id+"F0.wireOp",EDGE,"E1.bottom");var subQ7=sQuery(id+"F0.wireOp",EDGE,"E1.right");var subQ8=sQuery(id+"F0.wireOp",EDGE,"E1.top");var subQ9=sQuery(id+"F0.wireOp",EDGE,"E1.left");var subQ10=sQuery(id+"F0.wireOp",EDGE,"E23.filletArc");var subQ11=sQuery(id+"F0.wireOp",EDGE,"E24.filletArc");Q0=makeQuery(id+"F2.boolean.opBoolean","SPLIT",FACE,{"disambiguationData":[TD([makeQuery(id+"F1.opExtrude","SWEPT_FACE",FACE,{"disambiguationData":[OSD([subQ6])]})])],"derivedFrom":makeQuery(id+"F1.opExtrude","CAP_FACE",FACE,{"disambiguationData":[OSD([subQ6,subQ8,subQ9,subQ7,subQ4,subQ3,subQ2,subQ1,subQ0,subQ5,subQ10,subQ11])],"isStart":true})});}
            var sketch = newSketch(context, id + "F16", { "sketchPlane" : qUnion([Q0])});
            skSolve(sketch);
        }
        {
            var Q0;
            Q0=makeQuery(id+"F16.imprint","IMPRINT",FACE,{"disambiguationData":[TD([[makeQuery(id+"F16.imprint","IMPRINT",EDGE,{"derivedFrom":makeQuery(id+"F2.opExtrude","CAP_EDGE",EDGE,{"disambiguationData":[OSD([sQuery(id+"F0.wireOp",EDGE,"E12")])],"isStart":true})}),1.0]])]});
            var sketch = newSketch(context, id + "F17", { "sketchPlane" : qUnion([Q0])});
            skLineSegment(sketch, "E79.0", {"start": v(-70, 90) * mm, "end": v(70, 90) * mm});
            skArc(sketch, "E79.1", {"start": v(-70, 90) * mm, "mid": v(-77.07, 87.07) * mm, "end": v(-80, 80) * mm});
            skLineSegment(sketch, "E79.2", {"start": v(-80, -80) * mm, "end": v(-80, 80) * mm});
            skCircle(sketch, "E79.3", {"center": v(-60, 67.5) * mm, "radius": 4 * mm});
            skArc(sketch, "E79.4", {"start": v(56.15, 48.18) * mm, "mid": v(0, 67.5) * mm, "end": v(-56.15, 48.18) * mm});
            skArc(sketch, "E79.5", {"start": v(-56.15, 48.18) * mm, "mid": v(-58.99, 44.68) * mm, "end": v(-60, 40.3) * mm});
            skLineSegment(sketch, "E79.6", {"start": v(-60, 40.3) * mm, "end": v(-60, -40.3) * mm});
            skArc(sketch, "E79.7", {"start": v(80, 80) * mm, "mid": v(77.07, 87.07) * mm, "end": v(70, 90) * mm});
            skCircle(sketch, "E79.8", {"center": v(60, 67.5) * mm, "radius": 4 * mm});
            skLineSegment(sketch, "E79.9", {"start": v(80, -80) * mm, "end": v(80, 80) * mm});
            skLineSegment(sketch, "E79.10", {"start": v(60, 40.3) * mm, "end": v(60, -40.3) * mm});
            skArc(sketch, "E79.11", {"start": v(60, 40.3) * mm, "mid": v(58.99, 44.68) * mm, "end": v(56.15, 48.18) * mm});
            skArc(sketch, "E79.12", {"start": v(-80, -80) * mm, "mid": v(-77.07, -87.07) * mm, "end": v(-70, -90) * mm});
            skArc(sketch, "E79.13", {"start": v(-56.15, -48.18) * mm, "mid": v(0, -67.5) * mm, "end": v(56.15, -48.18) * mm});
            skArc(sketch, "E79.14", {"start": v(-60, -40.3) * mm, "mid": v(-58.99, -44.68) * mm, "end": v(-56.15, -48.18) * mm});
            skCircle(sketch, "E79.15", {"center": v(-60, -67.5) * mm, "radius": 4 * mm});
            skLineSegment(sketch, "E79.16", {"start": v(-70, -90) * mm, "end": v(70, -90) * mm});
            skArc(sketch, "E79.17", {"start": v(70, -90) * mm, "mid": v(77.07, -87.07) * mm, "end": v(80, -80) * mm});
            skArc(sketch, "E79.18", {"start": v(56.15, -48.18) * mm, "mid": v(58.99, -44.68) * mm, "end": v(60, -40.3) * mm});
            skCircle(sketch, "E80.0", {"center": v(60, -67.5) * mm, "radius": 4 * mm});
            skLineSegment(sketch, "E81", {"start": v(0, 120) * mm, "end": v(0, 90) * mm, "construction": true});
            skCircle(sketch, "E82", {"center": v(0, 120) * mm, "radius": 6 * mm});
            skLineSegment(sketch, "E83", {"start": v(-33, 90) * mm, "end": v(-15, 108) * mm});
            skLineSegment(sketch, "E84", {"start": v(-15, 108) * mm, "end": v(-15, 120) * mm});
            skLineSegment(sketch, "E85", {"start": v(15, 120) * mm, "end": v(15, 108) * mm});
            skLineSegment(sketch, "E86", {"start": v(15, 108) * mm, "end": v(33, 90) * mm});
            skArc(sketch, "E87", {"start": v(15, 120) * mm, "mid": v(0, 135) * mm, "end": v(-15, 120) * mm});
            skLineSegment(sketch, "E88", {"start": v(-80, 0) * mm, "end": v(80, 0) * mm, "construction": true});
            skLineSegment(sketch, "E89.MirrorCS", {"start": v(-33, -90) * mm, "end": v(-15, -108) * mm});
            skLineSegment(sketch, "E90.MirrorCS", {"start": v(-15, -108) * mm, "end": v(-15, -120) * mm});
            skArc(sketch, "E91.MirrorCS", {"start": v(15, -120) * mm, "mid": v(0, -135) * mm, "end": v(-15, -120) * mm});
            skLineSegment(sketch, "E92.MirrorCS", {"start": v(15, -120) * mm, "end": v(15, -108) * mm});
            skLineSegment(sketch, "E93.MirrorCS", {"start": v(15, -108) * mm, "end": v(33, -90) * mm});
            skCircle(sketch, "E94.MirrorC", {"center": v(0, -120) * mm, "radius": 6 * mm});
            skSolve(sketch);
        }
        {
            var Q0;
            Q0=makeQuery(id+"F17.imprint","IMPRINT",FACE,{"disambiguationData":[TD([[makeQuery(id+"F17.imprint","IMPRINT",EDGE,{"derivedFrom":sQuery(id+"F17.wireOp",EDGE,"E82")}),-1.0]])]});
            var Q1;
            Q1=makeQuery(id+"F16.imprint","IMPRINT",FACE,{"disambiguationData":[TD([[makeQuery(id+"F16.imprint","IMPRINT",EDGE,{"derivedFrom":makeQuery(id+"F1.opExtrude","CAP_EDGE",EDGE,{"disambiguationData":[OSD([sQuery(id+"F0.wireOp",EDGE,"E1.bottom")])],"isStart":true})}),1.0]])]});
            var Q2;
            {var subQ0=sQuery(id+"F17.wireOp",EDGE,"E89.MirrorCS");Q2=makeQuery(id+"F17.imprint","IMPRINT",FACE,{"disambiguationData":[TD([[makeQuery(id+"F17.imprint","IMPRINT",EDGE,{"derivedFrom":subQ0}),1.0]])]});}
            var Q3;
            Q3=makeQuery(id+"F2.opExtrude","CAP_FACE",FACE,{"disambiguationData":[OSD([sQuery(id+"F0.wireOp",EDGE,"E12"),sQuery(id+"F0.wireOp",EDGE,"E13"),sQuery(id+"F0.wireOp",EDGE,"E14"),sQuery(id+"F0.wireOp",EDGE,"E15"),sQuery(id+"F0.wireOp",EDGE,"E17.filletArc"),sQuery(id+"F0.wireOp",EDGE,"E18.filletArc"),sQuery(id+"F0.wireOp",EDGE,"E19.filletArc"),sQuery(id+"F0.wireOp",EDGE,"E20.filletArc"),sQuery(id+"F0.wireOp",EDGE,"E25.0"),sQuery(id+"F0.wireOp",EDGE,"E25.1"),sQuery(id+"F0.wireOp",EDGE,"E25.2"),sQuery(id+"F0.wireOp",EDGE,"E25.3"),sQuery(id+"F0.wireOp",EDGE,"E25.4"),sQuery(id+"F0.wireOp",EDGE,"E25.5"),sQuery(id+"F0.wireOp",EDGE,"E25.6"),sQuery(id+"F0.wireOp",EDGE,"E25.7")])],"isStart":false});
            extrude(context, id + "F18", {"entities" : qUnion([Q0, Q1, Q2]), "endBound" : BoundingType.UP_TO_SURFACE, "endBoundEntityFace" : qUnion([Q3]), "depth" : 25 * mm});
        }
    });
